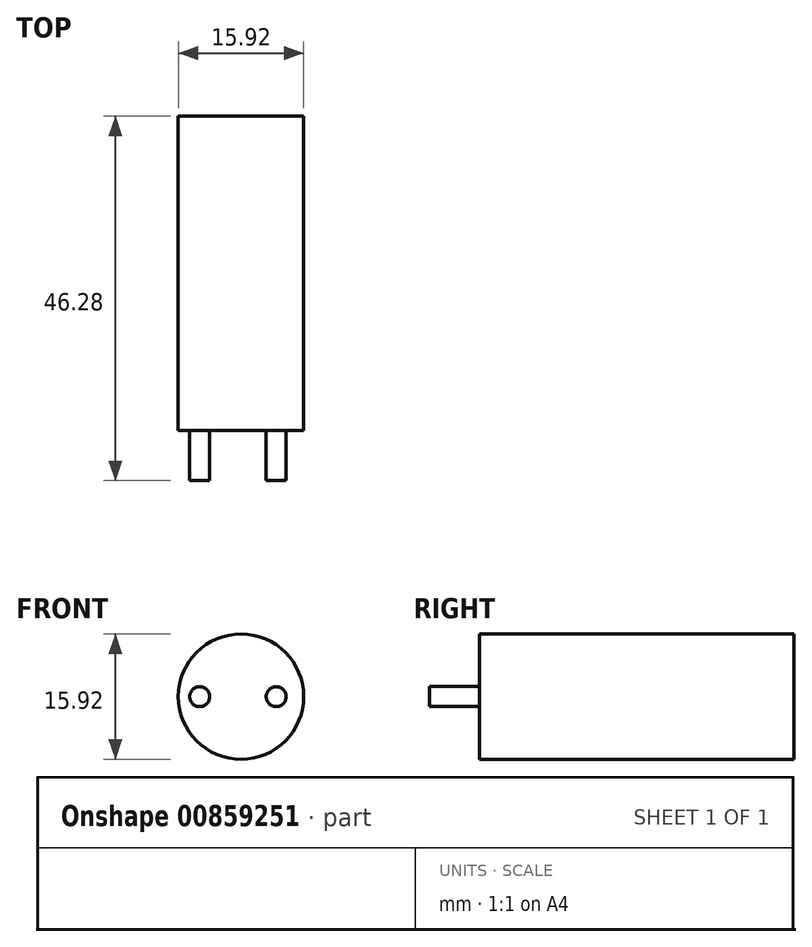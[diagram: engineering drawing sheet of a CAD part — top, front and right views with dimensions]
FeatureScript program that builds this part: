
annotation { "Feature Type Name" : "Feature", "Feature Type Description" : "" }
export const myFeature = defineFeature(function(context is Context, id is Id, definition is map)
    precondition{}
    {
        {
            var Q0;
            Q0=qCreatedBy(makeId("Front.planeOp"),FACE);
            var sketch = newSketch(context, id + "F0", { "sketchPlane" : qUnion([Q0])});
            skCircle(sketch, "E0", {"center": v(0, 0) * mm, "radius": 7.96 * mm});
            skSolve(sketch);
        }
        {
            var Q0;
            Q0 = qSketchRegion(id + "F0", true);
            extrude(context, id + "F1", {"entities" : qUnion([Q0]), "depth" : 39.93 * mm, "offsetDistance" : 25.4 * mm});
        }
        {
            var Q0;
            Q0=makeQuery(id+"F1.opExtrude","CAP_FACE",FACE,{"disambiguationData":[OSD([sQuery(id+"F0.wireOp",EDGE,"E0")])],"isStart":false});
            var sketch = newSketch(context, id + "F2", { "sketchPlane" : qUnion([Q0])});
            skCircle(sketch, "E1", {"center": v(-5.25, 0) * mm, "radius": 1.27 * mm});
            skCircle(sketch, "E2", {"center": v(4.48, 0) * mm, "radius": 1.27 * mm});
            skSolve(sketch);
        }
        {
            var Q0;
            Q0 = qSketchRegion(id + "F2", true);
            extrude(context, id + "F3", {"entities" : qUnion([Q0]), "operationType" : NewBodyOperationType.ADD, "depth" : 6.35 * mm, "offsetDistance" : 25.4 * mm});
        }
    });
